# Revit family: Picture-PGT-Aluminum-PW720d
name_source: partatom
category: Windows
revit_build: Autodesk Revit 2015 (Build: 20160512_1515(x64)
units: mm (PartAtom-declared; Revit-internal decimal feet)

## types (1)
- No Grid
    Analytic Construction = <None>
    Assembly Code = B2020.20
    BPTB Calc = 9 9/16"
    Color Glass = Glass - PGT - Clear
    Construction Type = Extruded Aluminum
    Custom Design Note = The types included show default grid/size configurations.  Please reference the 'Product Style Guide' to see all standard configurations and restrictions before creating custom designs.  Please contact PGT Industries with any questions regarding custom designs.
    Default Sill Height = 36"
    Description = Aluminum Picture Window
    Finish = Metal - PGT - Paint - White
    Grid = No
    Grid Layout Note = To edit the grid layout ensure the 'Grid' parameter is turned on and then select an option from the 'Grid Type' drop down.  Please refer to the 'Product Style Guide' for standard configurations and restrictions.
    Grid Type = Face_Based_Mullion_1inch Glass : BP
    Height = 60"
    Height Calc = 57 1/4"
    Manufacturer = PGT Industries
    Maximum Size = Up to 145” Width OR Height
    Minimum Size = 14 1/2” x 14 1/2”
    Model = PW720
    Product Page URL = http://www.pgtindustries.com
    Product Style Guide = http://www.pgtindustries.com
    Rough Height = 60"
    Rough Width = 60"
    Type Comments = O Flange
    URL = http://www.pgtindustries.com
    Wall Closure = By host
    Width = 60"
    Width Calc = 57 1/4"

## geometry (parser evidence)
native form markers: Sweep x16
no freeform markers — native parametric forms only
